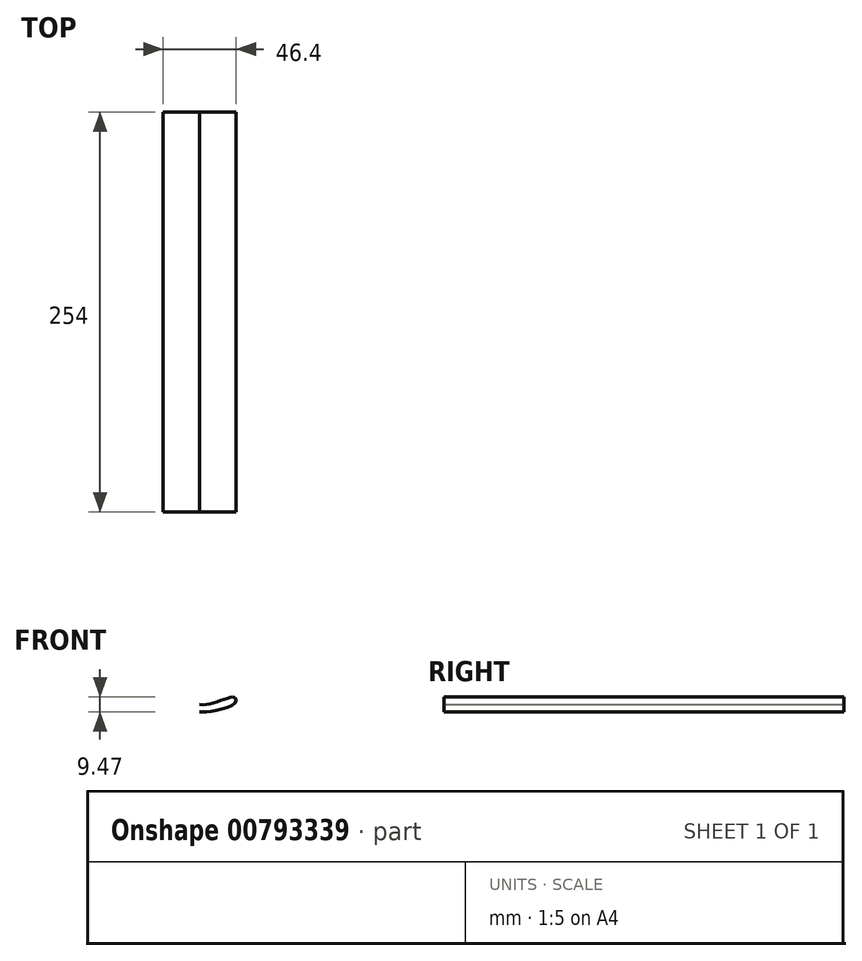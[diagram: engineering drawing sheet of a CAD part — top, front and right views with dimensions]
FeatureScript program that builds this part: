
annotation { "Feature Type Name" : "Feature", "Feature Type Description" : "" }
export const myFeature = defineFeature(function(context is Context, id is Id, definition is map)
    precondition{}
    {
        {
            var Q0;
            Q0=qCreatedBy(makeId("Front.planeOp"),FACE);
            var sketch = newSketch(context, id + "F0", { "sketchPlane" : qUnion([Q0])});
            skFitSpline(sketch, "E0", {"points": [v(0, 4.57) * mm, v(-9.57, 5.97) * mm, v(-19.06, 9) * mm, v(-22.23, 9.13) * mm, v(-22.66, 5.68) * mm, v(-4.1, 0) * mm, v(0, 0) * mm], "startDerivative": vector(-50.15, -3.9) * mm, "endDerivative": vector(46.82, -5.4) * mm});
            skFitSpline(sketch, "E1.MirrorCS", {"points": [v(0, 4.57) * mm, v(9.57, 5.97) * mm, v(19.06, 9) * mm, v(22.23, 9.13) * mm, v(22.66, 5.68) * mm, v(4.1, 0) * mm, v(0, 0) * mm], "startDerivative": vector(50.15, -3.9) * mm, "endDerivative": vector(-46.82, -5.4) * mm});
            skSolve(sketch);
        }
        {
            var Q0;
            Q0 = qSketchRegion(id + "F0", true);
            extrude(context, id + "F1", {"entities" : qUnion([Q0]), "depth" : 254 * mm, "offsetDistance" : 25.4 * mm});
        }
    });
